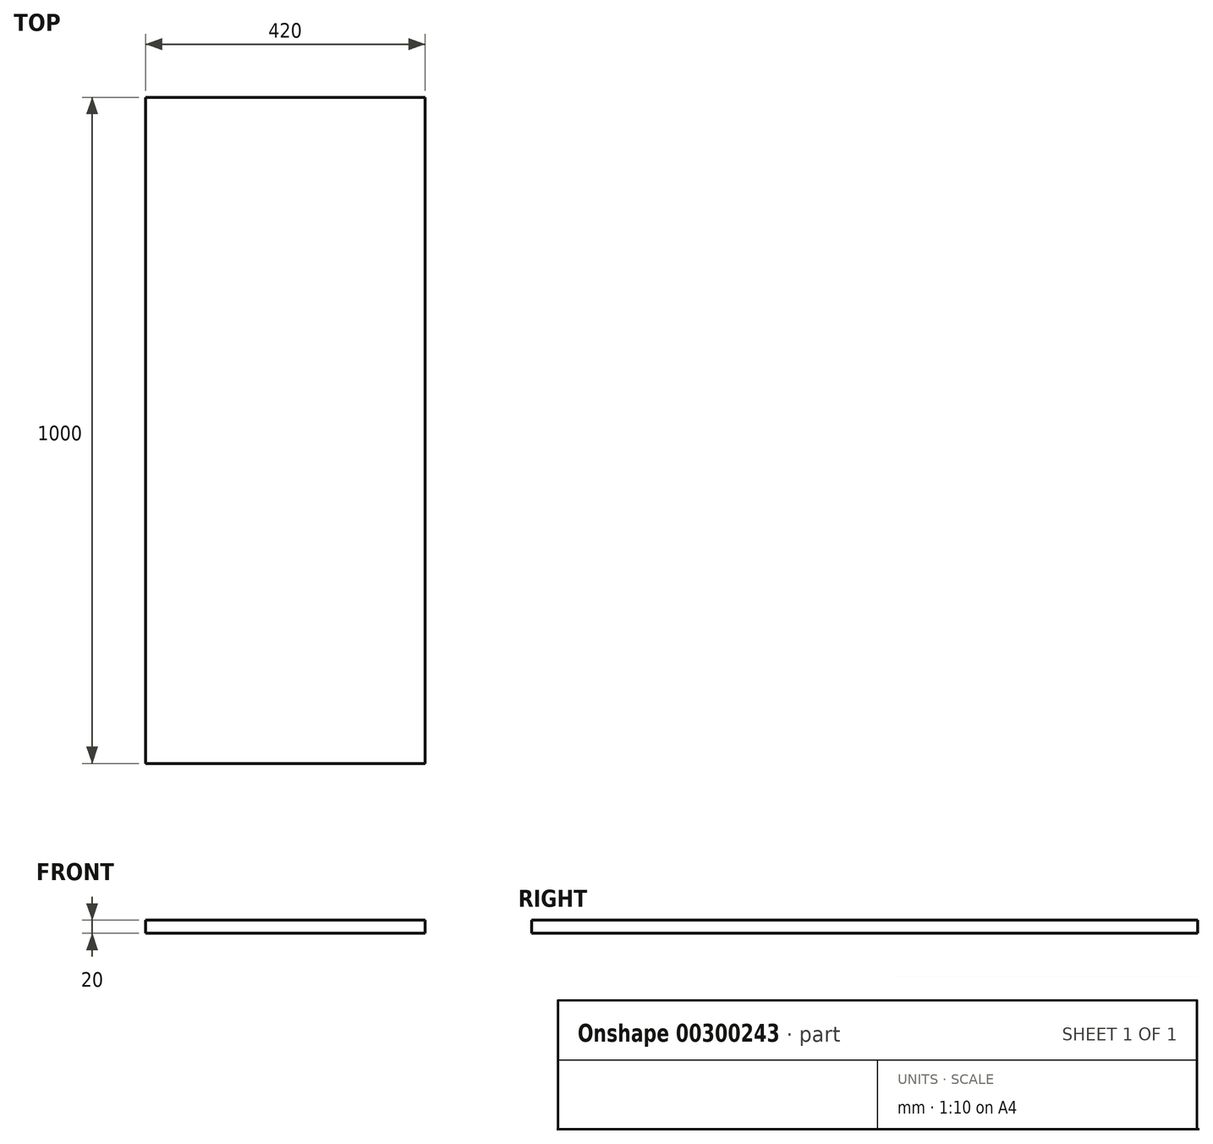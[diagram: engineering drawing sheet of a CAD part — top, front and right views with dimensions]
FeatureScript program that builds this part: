
annotation { "Feature Type Name" : "Feature", "Feature Type Description" : "" }
export const myFeature = defineFeature(function(context is Context, id is Id, definition is map)
    precondition{}
    {
        {
            var Q0;
            Q0=qCreatedBy(makeId("Top.planeOp"),FACE);
            var sketch = newSketch(context, id + "F0", { "sketchPlane" : qUnion([Q0])});
            skLineSegment(sketch, "E0.bottom", {"start": v(210, 500) * mm, "end": v(-210, 500) * mm});
            skLineSegment(sketch, "E0.top", {"start": v(210, -500) * mm, "end": v(-210, -500) * mm});
            skLineSegment(sketch, "E0.left", {"start": v(210, 500) * mm, "end": v(210, -500) * mm});
            skLineSegment(sketch, "E0.right", {"start": v(-210, 500) * mm, "end": v(-210, -500) * mm});
            skPoint(sketch, "E0.middle", {"position": v(0, 0) * mm});
            skSolve(sketch);
        }
        {
            var Q0;
            Q0=makeQuery(id+"F0.imprint","IMPRINT",FACE,{"disambiguationData":[TD([[makeQuery(id+"F0.imprint","IMPRINT",EDGE,{"derivedFrom":sQuery(id+"F0.wireOp",EDGE,"E0.bottom")}),1.0]])]});
            extrude(context, id + "F1", {"entities" : qUnion([Q0]), "depth" : 20 * mm});
        }
    });
